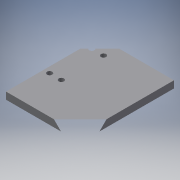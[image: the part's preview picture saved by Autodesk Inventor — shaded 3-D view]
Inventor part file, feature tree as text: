
AUTODESK INVENTOR PART (.ipt)
format: ipt  version: 2016 (Build 200138000, 138)  size: 124,928 bytes
history: native  units: mm
features: reference x4, extrude x3, sketch x3, fillet x1
ambient origin geometry x8: Origin, YZ Plane, XZ Plane, XY Plane, X Axis, Y Axis, Z Axis, Center Point
bodies: Solid1 (feature_tree)
feature tree (11):
  extrude  "Extrusion1"  Depth=95.0mm
  extrude  "Extrusion3"  Depth=7.0mm
  fillet  "Fillet1"  Radius=35.0mm
  extrude  "Extrusion4"  Depth=3.0mm TaperAngle=0.0deg
  sketch  "Sketch1"  dims[d0=120.0mm d1=95.0mm]
  sketch  "Sketch3"  dims[d2=6.0mm d3=0.0mm d9=7.0mm d10=35.0mm]
  sketch  "Sketch4"  dims[d11=75.0mm d12=3.0mm d13=0.0mm d14=7.0mm d15=10.0mm d16=0.0mm]
  reference  "Reference1"
  reference  "Reference2"
  reference  "Reference3"
  reference  "Reference4"
